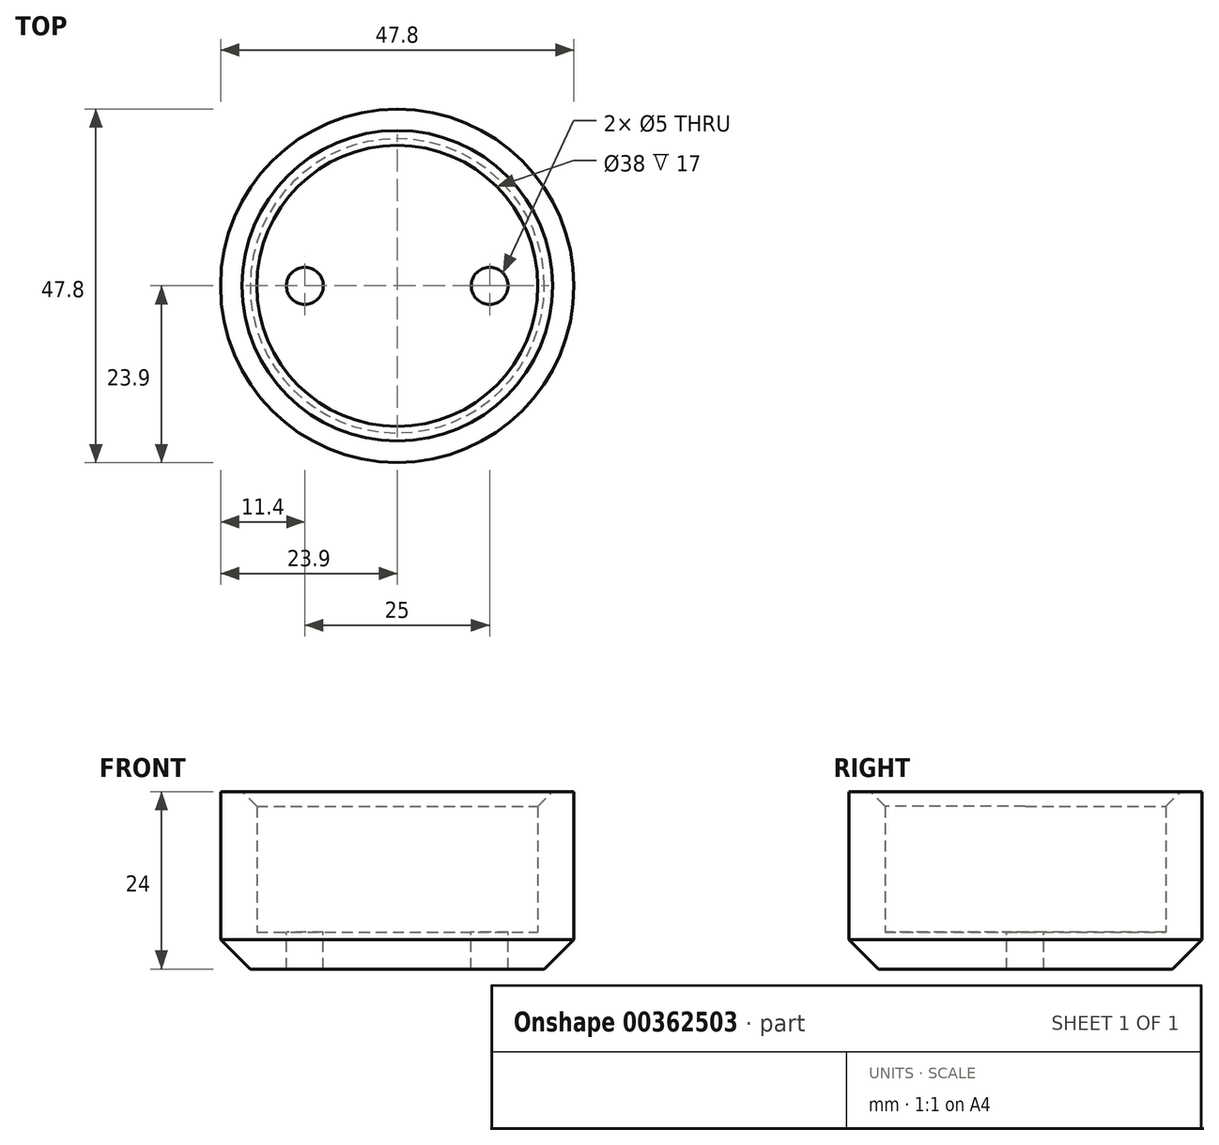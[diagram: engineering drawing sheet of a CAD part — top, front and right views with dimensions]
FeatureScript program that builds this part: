
annotation { "Feature Type Name" : "Feature", "Feature Type Description" : "" }
export const myFeature = defineFeature(function(context is Context, id is Id, definition is map)
    precondition{}
    {
        {
            var Q0;
            Q0=qCreatedBy(makeId("Front.planeOp"),FACE);
            var sketch = newSketch(context, id + "F0", { "sketchPlane" : qUnion([Q0])});
            skLineSegment(sketch, "E0", {"start": v(0, 0) * mm, "end": v(23.9, 0) * mm});
            skLineSegment(sketch, "E1", {"start": v(23.9, 0) * mm, "end": v(23.9, 24) * mm});
            skLineSegment(sketch, "E2", {"start": v(23.9, 24) * mm, "end": v(19, 24) * mm});
            skLineSegment(sketch, "E3", {"start": v(19, 24) * mm, "end": v(19, 5) * mm});
            skLineSegment(sketch, "E4", {"start": v(19, 5) * mm, "end": v(0, 5) * mm});
            skLineSegment(sketch, "E5", {"start": v(0, 5) * mm, "end": v(0, 0) * mm});
            skPoint(sketch, "E6.0", {"position": v(0, 0) * mm});
            skLineSegment(sketch, "E7", {"start": v(0, -21.56) * mm, "end": v(0, 46.3) * mm, "construction": true});
            skSolve(sketch);
        }
        {
            var Q0;
            Q0 = qSketchRegion(id + "F0", true);
            var Q1;
            Q1=sQuery(id+"F0.wireOp",EDGE,"E7");
            revolve(context, id + "F1", {"entities" : qUnion([Q0]), "axis" : qUnion([Q1]), "revolveType" : RevolveType.FULL});
        }
        {
            var Q0;
            Q0=makeQuery(id+"F1.opRevolve","SWEPT_EDGE",EDGE,{"disambiguationData":[OSD([sQuery(id+"F0.wireOp",EDGE,"E2"),sQuery(id+"F0.wireOp",EDGE,"E3")])]});
            chamfer(context, id + "F2", {"entities" : qUnion([Q0]), "width" : 2 * mm, "tangentPropagation" : true});
        }
        {
            var Q0;
            Q0=makeQuery(id+"F1.opRevolve","SWEPT_EDGE",EDGE,{"disambiguationData":[OSD([sQuery(id+"F0.wireOp",EDGE,"E0"),sQuery(id+"F0.wireOp",EDGE,"E1")])]});
            chamfer(context, id + "F3", {"entities" : qUnion([Q0]), "width" : 4 * mm, "tangentPropagation" : true});
        }
        {
            var Q0;
            Q0=makeQuery(id+"F1.opRevolve","SWEPT_FACE",FACE,{"disambiguationData":[OSD([sQuery(id+"F0.wireOp",EDGE,"E4")])]});
            var sketch = newSketch(context, id + "F4", { "sketchPlane" : qUnion([Q0])});
            skPoint(sketch, "E8", {"position": v(12.5, 0) * mm});
            skPoint(sketch, "E9", {"position": v(-12.5, 0) * mm});
            skLineSegment(sketch, "E10", {"start": v(0, 12.35) * mm, "end": v(0, -11.06) * mm, "construction": true});
            skSolve(sketch);
        }
        {
            var Q0;
            Q0=sQuery(id+"F4.wireOp",VERTEX,"E9");
            var Q1;
            Q1=sQuery(id+"F4.wireOp",VERTEX,"E8");
            var Q2;
            Q2=makeQuery(id+"F1.opRevolve","SWEPT_BODY",BODY,{"disambiguationData":[OSD([sQuery(id+"F0.wireOp",EDGE,"E0"),sQuery(id+"F0.wireOp",EDGE,"E1"),sQuery(id+"F0.wireOp",EDGE,"E2"),sQuery(id+"F0.wireOp",EDGE,"E3"),sQuery(id+"F0.wireOp",EDGE,"E4"),sQuery(id+"F0.wireOp",EDGE,"E5")])]});
            hole(context, id + "F5", {"style" : HoleStyle.SIMPLE, "endStyle" : HoleEndStyle.THROUGH, "standardTappedOrClearance" : lookupTablePath({ "standard" : "ISO", "engagement" : "75%", "pitch" : "1 mm", "size" : "M6", "type" : "Tapped" }), "standardBlindInLast" : lookupTablePath({ "standard" : "ISO", "engagement" : "75%", "pitch" : "1 mm", "size" : "M6", "type" : "Tapped" }), "holeDiameter" : 5 * mm, "showTappedDepth" : true, "isTappedThrough" : true, "tappedDepth" : 12 * mm, "tapClearance" : 3, "locations" : qUnion([Q0, Q1]), "scope" : qUnion([Q2]), "majorDiameter" : 6 * mm});
        }
    });
